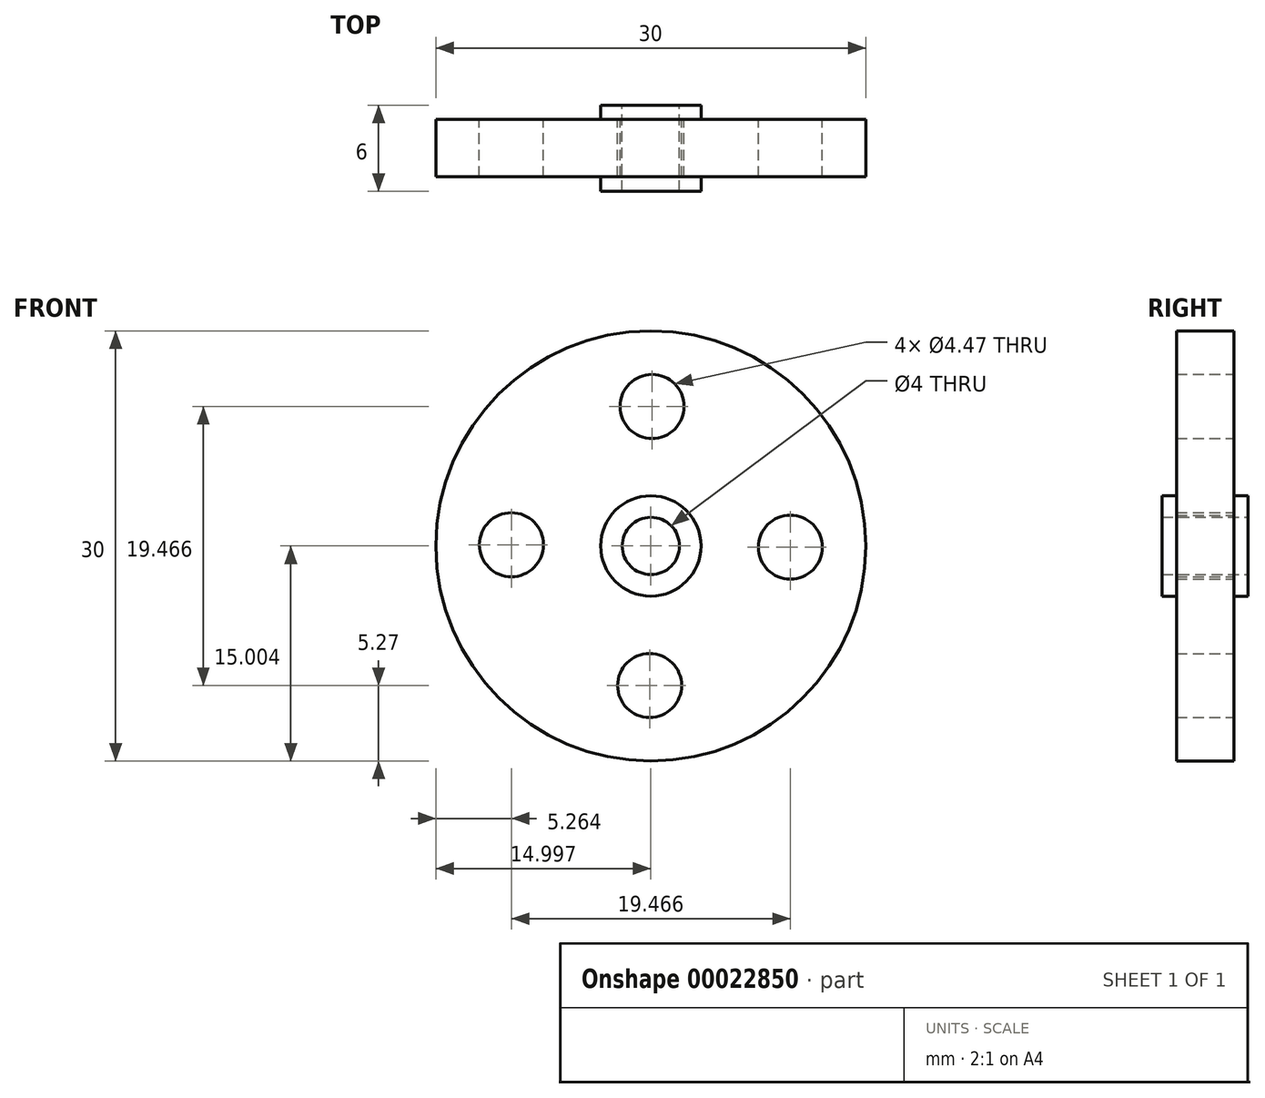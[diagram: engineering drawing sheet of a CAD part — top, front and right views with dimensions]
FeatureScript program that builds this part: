
annotation { "Feature Type Name" : "Feature", "Feature Type Description" : "" }
export const myFeature = defineFeature(function(context is Context, id is Id, definition is map)
    precondition{}
    {
        {
            var Q0;
            Q0=qCreatedBy(makeId("Front.planeOp"),FACE);
            var sketch = newSketch(context, id + "F0", { "sketchPlane" : qUnion([Q0])});
            skCircle(sketch, "E0", {"center": v(-3.81, -2.79) * mm, "radius": 15 * mm});
            skCircle(sketch, "E1", {"center": v(-3.81, -2.79) * mm, "radius": 3.5 * mm});
            skCircle(sketch, "E2", {"center": v(-3.81, -2.79) * mm, "radius": 2 * mm});
            skCircle(sketch, "E3", {"center": v(-3.73, 6.95) * mm, "radius": 2.23 * mm});
            skCircle(sketch, "E4.1.0", {"center": v(-13.55, -2.7) * mm, "radius": 2.23 * mm});
            skCircle(sketch, "E4.2.0", {"center": v(-3.9, -12.52) * mm, "radius": 2.23 * mm});
            skCircle(sketch, "E4.3.0", {"center": v(5.92, -2.87) * mm, "radius": 2.23 * mm});
            skSolve(sketch);
        }
        {
            var Q0;
            Q0=qSketchRegion(id+"F0",true);
            extrude(context, id + "F1", {"entities" : qUnion([Q0]), "endBound" : BoundingType.SYMMETRIC, "depth" : 4 * mm});
        }
        {
            var Q0;
            Q0=makeQuery(id+"F0.imprint","IMPRINT",FACE,{"disambiguationData":[TD([[makeQuery(id+"F0.imprint","IMPRINT",EDGE,{"derivedFrom":sQuery(id+"F0.wireOp",EDGE,"E1")}),1.0]])]});
            extrude(context, id + "F2", {"entities" : qUnion([Q0]), "operationType" : NewBodyOperationType.ADD, "endBound" : BoundingType.SYMMETRIC, "depth" : 6 * mm});
        }
    });
